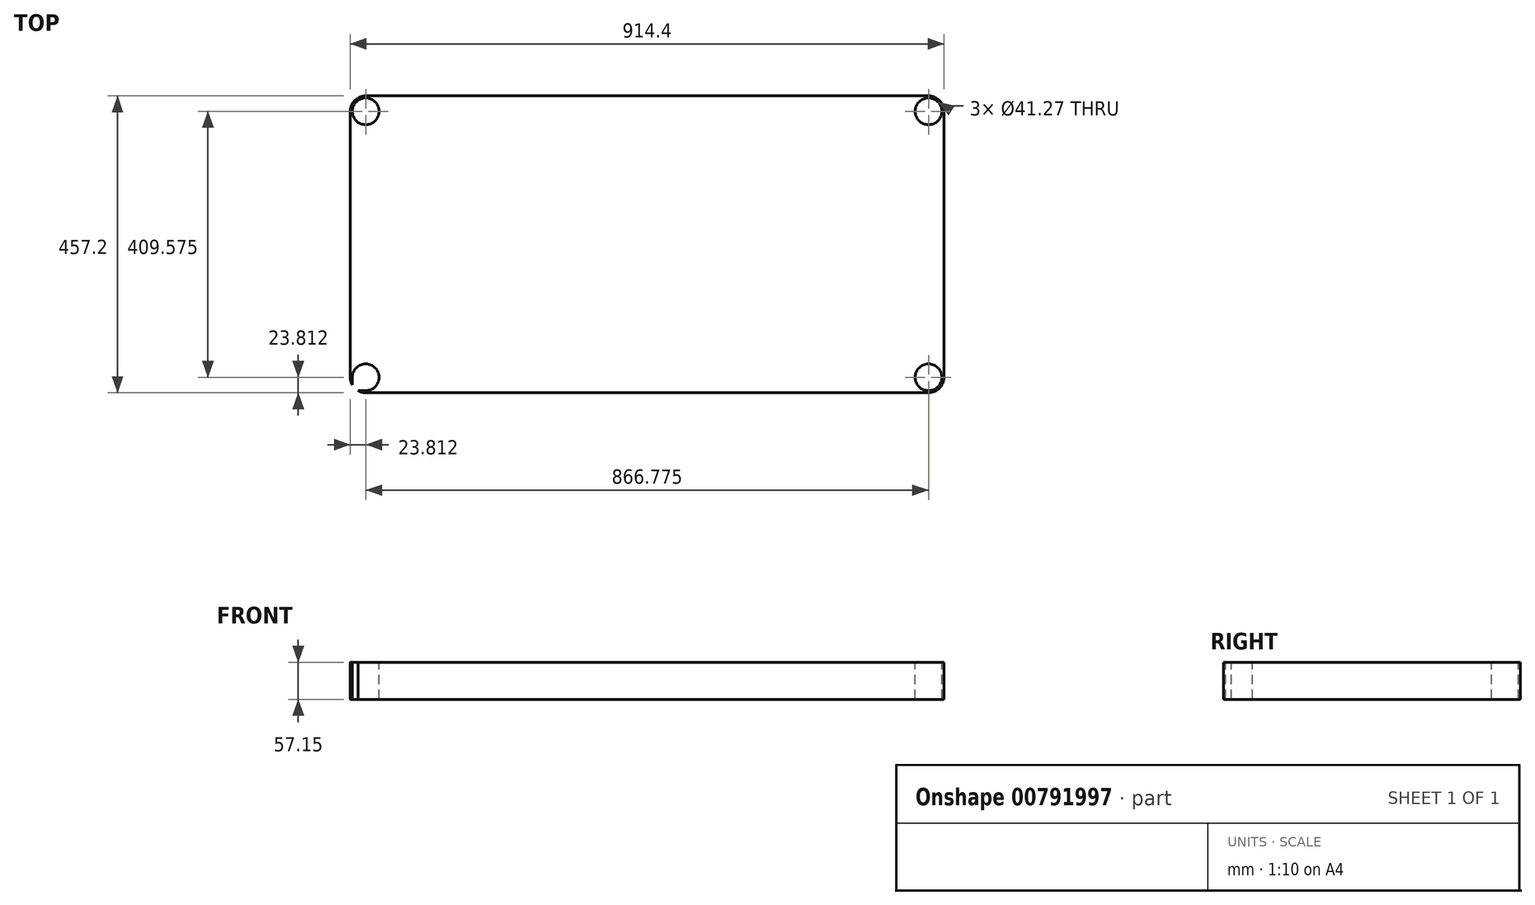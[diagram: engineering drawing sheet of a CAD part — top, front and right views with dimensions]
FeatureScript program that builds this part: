
annotation { "Feature Type Name" : "Feature", "Feature Type Description" : "" }
export const myFeature = defineFeature(function(context is Context, id is Id, definition is map)
    precondition{}
    {
        {
            assignVariable(context, id + "F0", {"name" : "height", "anyValue" : 57.15 * mm});
        }
        {
            assignVariable(context, id + "F1", {"name" : "thick", "anyValue" : 1 / 203.2 * mm});
        }
        {
            var Q0;
            Q0=qCreatedBy(makeId("Top.planeOp"),FACE);
            var sketch = newSketch(context, id + "F2", { "sketchPlane" : qUnion([Q0])});
            skLineSegment(sketch, "E0.bottom", {"start": v(0, 0) * mm, "end": v(914.4, 0) * mm});
            skLineSegment(sketch, "E0.top", {"start": v(0, 457.2) * mm, "end": v(914.4, 457.2) * mm});
            skLineSegment(sketch, "E0.left", {"start": v(0, 0) * mm, "end": v(0, 457.2) * mm});
            skLineSegment(sketch, "E0.right", {"start": v(914.4, 0) * mm, "end": v(914.4, 457.2) * mm});
            skSolve(sketch);
        }
        {
            var Q0;
            Q0=makeQuery(id+"F2.imprint","IMPRINT",FACE,{"disambiguationData":[TD([[makeQuery(id+"F2.imprint","IMPRINT",EDGE,{"derivedFrom":sQuery(id+"F2.wireOp",EDGE,"E0.bottom")}),1.0]])]});
            extrude(context, id + "F3", {"entities" : qUnion([Q0]), "depth" : getVariable(context, 'height'), "offsetDistance" : 25.4 * mm});
        }
        {
            var Q0;
            Q0=makeQuery(id+"F3.opExtrude","CAP_FACE",FACE,{"disambiguationData":[OSD([sQuery(id+"F2.wireOp",EDGE,"E0.bottom"),sQuery(id+"F2.wireOp",EDGE,"E0.top"),sQuery(id+"F2.wireOp",EDGE,"E0.left"),sQuery(id+"F2.wireOp",EDGE,"E0.right")])],"isStart":false});
            var sketch = newSketch(context, id + "F4", { "sketchPlane" : qUnion([Q0])});
            skPoint(sketch, "E1", {"position": v(3.18, 3.18) * mm});
            skPoint(sketch, "E2", {"position": v(3.18, 454.02) * mm});
            skPoint(sketch, "E3", {"position": v(911.23, 454.03) * mm});
            skPoint(sketch, "E4", {"position": v(911.23, 3.18) * mm});
            skLineSegment(sketch, "E5", {"start": v(3.17, 3.18) * mm, "end": v(911.23, 3.18) * mm});
            skLineSegment(sketch, "E6", {"start": v(911.23, 3.18) * mm, "end": v(911.23, 454.03) * mm});
            skLineSegment(sketch, "E7", {"start": v(911.23, 454.03) * mm, "end": v(3.17, 454.02) * mm});
            skLineSegment(sketch, "E8", {"start": v(3.17, 454.02) * mm, "end": v(3.17, 3.18) * mm});
            skLineSegment(sketch, "E9.0", {"start": v(0, 0) * mm, "end": v(0, 457.2) * mm});
            skLineSegment(sketch, "E10.0.0", {"start": v(914.4, 457.2) * mm, "end": v(0, 457.2) * mm});
            skLineSegment(sketch, "E10.0.1", {"start": v(0, 457.2) * mm, "end": v(0, 0) * mm});
            skLineSegment(sketch, "E10.0.2", {"start": v(0, 0) * mm, "end": v(914.4, 0) * mm});
            skLineSegment(sketch, "E10.0.3", {"start": v(914.4, 0) * mm, "end": v(914.4, 457.2) * mm});
            skCircle(sketch, "E11", {"center": v(23.81, 23.81) * mm, "radius": 23.81 * mm});
            skCircle(sketch, "E12", {"center": v(23.81, 433.39) * mm, "radius": 23.81 * mm});
            skCircle(sketch, "E13", {"center": v(890.59, 433.39) * mm, "radius": 23.81 * mm});
            skCircle(sketch, "E14", {"center": v(890.59, 23.81) * mm, "radius": 23.81 * mm});
            skCircle(sketch, "E15", {"center": v(23.81, 23.81) * mm, "radius": 20.64 * mm});
            skCircle(sketch, "E16", {"center": v(23.81, 433.39) * mm, "radius": 20.64 * mm});
            skCircle(sketch, "E17", {"center": v(890.59, 433.39) * mm, "radius": 20.64 * mm});
            skCircle(sketch, "E18", {"center": v(890.59, 23.81) * mm, "radius": 20.64 * mm});
            skSolve(sketch);
        }
        {
            var Q0;
            {var subQ3=sQuery(id+"F4.wireOp",EDGE,"E11");var subQ13=sQuery(id+"F4.wireOp",EDGE,"E5");var subQ15=makeQuery(id+"F4.imprint","INTERSECT",VERTEX,{"disambiguationData":[OD(1.0)],"derivedFrom":[subQ13,subQ3]});Q0=makeQuery(id+"F4.imprint","IMPRINT",FACE,{"disambiguationData":[TD([[makeQuery(id+"F4.imprint","IMPRINT",EDGE,{"disambiguationData":[TD([[subQ15,-1.0]])],"derivedFrom":subQ13}),1.0]])]});}
            extrude(context, id + "F5", {"entities" : qUnion([Q0]), "operationType" : NewBodyOperationType.REMOVE, "oppositeDirection" : true, "depth" : getVariable(context, 'height') - getVariable(context, 'thick'), "offsetDistance" : 25.4 * mm});
        }
        {
            var Q0;
            {var subQ6=sQuery(id+"F4.wireOp",EDGE,"E8");var subQ7=sQuery(id+"F4.wireOp",EDGE,"E5");var subQ8=makeQuery(id+"F4.imprint","INTERSECT",VERTEX,{"derivedFrom":[subQ7,subQ6]});Q0=makeQuery(id+"F4.imprint","IMPRINT",FACE,{"disambiguationData":[TD([[makeQuery(id+"F4.imprint","IMPRINT",EDGE,{"disambiguationData":[TD([[subQ8,-1.0]])],"derivedFrom":subQ7}),-1.0]])]});}
            var Q1;
            {var subQ0=sQuery(id+"F4.wireOp",EDGE,"E8");var subQ1=sQuery(id+"F4.wireOp",EDGE,"E5");var subQ2=makeQuery(id+"F4.imprint","INTERSECT",VERTEX,{"derivedFrom":[subQ1,subQ0]});Q1=makeQuery(id+"F4.imprint","IMPRINT",FACE,{"disambiguationData":[TD([[makeQuery(id+"F4.imprint","IMPRINT",EDGE,{"disambiguationData":[TD([[subQ2,-1.0]])],"derivedFrom":subQ1}),1.0]])]});}
            var Q2;
            {var subQ0=sQuery(id+"F4.wireOp",EDGE,"E15");var subQ1=makeQuery(id+"F4.imprint","INTERSECT",VERTEX,{"derivedFrom":[sQuery(id+"F4.wireOp",EDGE,"E5"),subQ0]});Q2=makeQuery(id+"F4.imprint","IMPRINT",FACE,{"disambiguationData":[TD([[makeQuery(id+"F4.imprint","IMPRINT",EDGE,{"disambiguationData":[TD([[subQ1,1.0]])],"derivedFrom":subQ0}),1.0]])]});}
            var Q3;
            {var subQ0=sQuery(id+"F4.wireOp",EDGE,"E16");var subQ1=makeQuery(id+"F4.imprint","INTERSECT",VERTEX,{"derivedFrom":[sQuery(id+"F4.wireOp",EDGE,"E7"),subQ0]});Q3=makeQuery(id+"F4.imprint","IMPRINT",FACE,{"disambiguationData":[TD([[makeQuery(id+"F4.imprint","IMPRINT",EDGE,{"disambiguationData":[TD([[subQ1,-1.0]])],"derivedFrom":subQ0}),1.0]])]});}
            var Q4;
            {var subQ0=sQuery(id+"F4.wireOp",EDGE,"E8");var subQ1=sQuery(id+"F4.wireOp",EDGE,"E7");var subQ2=makeQuery(id+"F4.imprint","INTERSECT",VERTEX,{"derivedFrom":[subQ1,subQ0]});Q4=makeQuery(id+"F4.imprint","IMPRINT",FACE,{"disambiguationData":[TD([[makeQuery(id+"F4.imprint","IMPRINT",EDGE,{"disambiguationData":[TD([[subQ2,1.0]])],"derivedFrom":subQ1}),1.0]])]});}
            var Q5;
            {var subQ6=sQuery(id+"F4.wireOp",EDGE,"E8");var subQ7=sQuery(id+"F4.wireOp",EDGE,"E7");var subQ8=makeQuery(id+"F4.imprint","INTERSECT",VERTEX,{"derivedFrom":[subQ7,subQ6]});Q5=makeQuery(id+"F4.imprint","IMPRINT",FACE,{"disambiguationData":[TD([[makeQuery(id+"F4.imprint","IMPRINT",EDGE,{"disambiguationData":[TD([[subQ8,1.0]])],"derivedFrom":subQ7}),-1.0]])]});}
            var Q6;
            {var subQ0=sQuery(id+"F4.wireOp",EDGE,"E7");var subQ1=sQuery(id+"F4.wireOp",EDGE,"E6");var subQ2=makeQuery(id+"F4.imprint","INTERSECT",VERTEX,{"derivedFrom":[subQ1,subQ0]});Q6=makeQuery(id+"F4.imprint","IMPRINT",FACE,{"disambiguationData":[TD([[makeQuery(id+"F4.imprint","IMPRINT",EDGE,{"disambiguationData":[TD([[subQ2,1.0]])],"derivedFrom":subQ1}),1.0]])]});}
            var Q7;
            {var subQ6=sQuery(id+"F4.wireOp",EDGE,"E6");var subQ8=sQuery(id+"F4.wireOp",EDGE,"E7");var subQ9=makeQuery(id+"F4.imprint","INTERSECT",VERTEX,{"derivedFrom":[subQ6,subQ8]});Q7=makeQuery(id+"F4.imprint","IMPRINT",FACE,{"disambiguationData":[TD([[makeQuery(id+"F4.imprint","IMPRINT",EDGE,{"disambiguationData":[TD([[subQ9,1.0]])],"derivedFrom":subQ6}),-1.0]])]});}
            var Q8;
            {var subQ0=sQuery(id+"F4.wireOp",EDGE,"E17");var subQ1=makeQuery(id+"F4.imprint","INTERSECT",VERTEX,{"derivedFrom":[sQuery(id+"F4.wireOp",EDGE,"E6"),subQ0]});Q8=makeQuery(id+"F4.imprint","IMPRINT",FACE,{"disambiguationData":[TD([[makeQuery(id+"F4.imprint","IMPRINT",EDGE,{"disambiguationData":[TD([[subQ1,-1.0]])],"derivedFrom":subQ0}),1.0]])]});}
            var Q9;
            {var subQ0=sQuery(id+"F4.wireOp",EDGE,"E6");var subQ1=sQuery(id+"F4.wireOp",EDGE,"E5");var subQ2=makeQuery(id+"F4.imprint","INTERSECT",VERTEX,{"derivedFrom":[subQ1,subQ0]});Q9=makeQuery(id+"F4.imprint","IMPRINT",FACE,{"disambiguationData":[TD([[makeQuery(id+"F4.imprint","IMPRINT",EDGE,{"disambiguationData":[TD([[subQ2,1.0]])],"derivedFrom":subQ1}),1.0]])]});}
            var Q10;
            {var subQ5=sQuery(id+"F4.wireOp",EDGE,"E6");var subQ6=sQuery(id+"F4.wireOp",EDGE,"E5");var subQ7=makeQuery(id+"F4.imprint","INTERSECT",VERTEX,{"derivedFrom":[subQ6,subQ5]});Q10=makeQuery(id+"F4.imprint","IMPRINT",FACE,{"disambiguationData":[TD([[makeQuery(id+"F4.imprint","IMPRINT",EDGE,{"disambiguationData":[TD([[subQ7,1.0]])],"derivedFrom":subQ6}),-1.0]])]});}
            var Q11;
            {var subQ0=sQuery(id+"F4.wireOp",EDGE,"E18");var subQ1=makeQuery(id+"F4.imprint","INTERSECT",VERTEX,{"derivedFrom":[sQuery(id+"F4.wireOp",EDGE,"E5"),subQ0]});Q11=makeQuery(id+"F4.imprint","IMPRINT",FACE,{"disambiguationData":[TD([[makeQuery(id+"F4.imprint","IMPRINT",EDGE,{"disambiguationData":[TD([[subQ1,1.0]])],"derivedFrom":subQ0}),1.0]])]});}
            extrude(context, id + "F6", {"entities" : qUnion([Q0, Q1, Q2, Q3, Q4, Q5, Q6, Q7, Q8, Q9, Q10, Q11]), "operationType" : NewBodyOperationType.REMOVE, "oppositeDirection" : true, "depth" : getVariable(context, 'height'), "offsetDistance" : 25.4 * mm});
        }
    });
